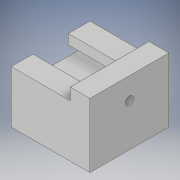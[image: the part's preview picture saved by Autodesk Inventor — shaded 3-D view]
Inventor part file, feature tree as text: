
AUTODESK INVENTOR PART (.ipt)
format: ipt  version: 2019 (Build 230136000, 136)  size: 125,440 bytes
history: native  units: in
note: dims shown in document units (in); Inventor stores cm internally (conversion verified against a paired STEP export)
features: extrude x3, sketch x3
ambient origin geometry x8: Origin, YZ Plane, XZ Plane, XY Plane, X Axis, Y Axis, Z Axis, Center Point
bodies: Solid1 (feature_tree)
feature tree (6):
  extrude  "Extrusion1"  Depth=0.45in
  extrude  "Extrusion2"  Depth=0.15in
  extrude  "Extrusion3"  Depth=0.125in
  sketch  "Sketch1"  dims[d0=1.0in d1=0.45in]
  sketch  "Sketch2"  dims[d2=0.75in d3=0.15in]
  sketch  "Sketch4"  dims[d4=0.275in d5=0.125in d6=0.25in d7=0.665in d8=0.75in d9=0.0in d10=0.15in d11=1.0in d12=0.25in d13=0.0in d21=0.104in d22=0.5in d23=0.125in d24=-0.0in d25=1.0in d26=0.0in]
